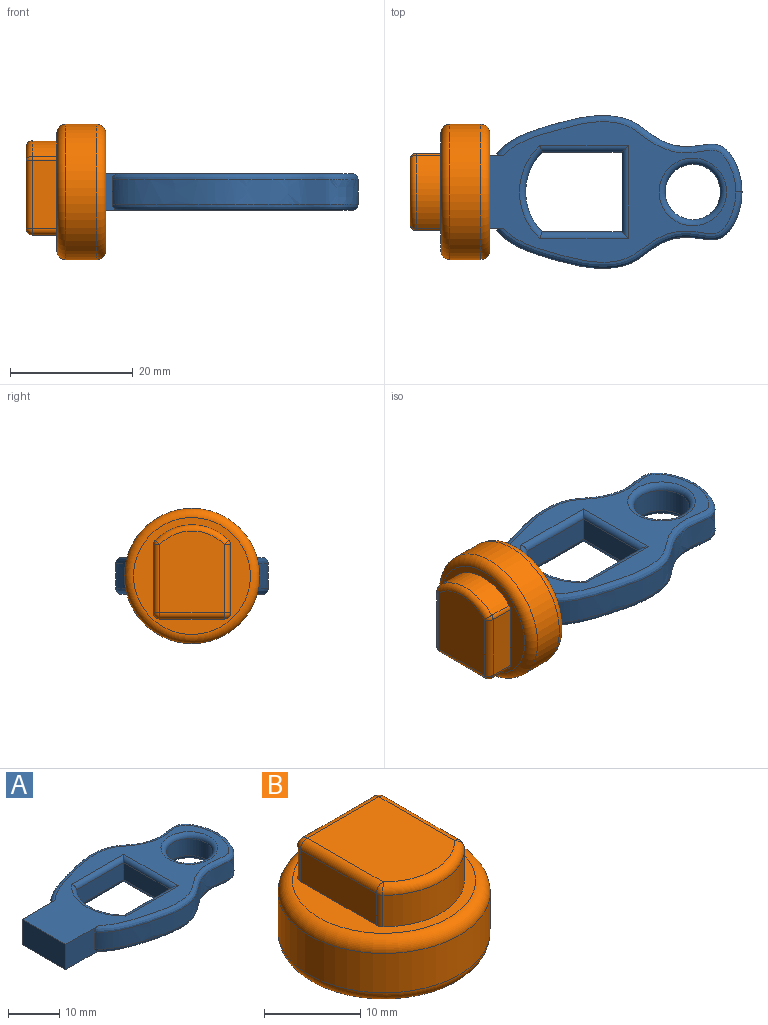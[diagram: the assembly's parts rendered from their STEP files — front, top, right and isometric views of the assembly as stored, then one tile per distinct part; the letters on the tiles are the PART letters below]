
ASSEMBLY  parts=2 mates=1
PART A: 26 faces, bbox 48.4x25.2x6.4 mm
  f0: plane 12x6mm, normal (-1,0,0), area 72mm2, adj f1,f9,f10,f11
  f1: plane 9.62x6.37mm, normal (0,-1,0), area 48.5mm2, adj f0,f2,f10,f11,f12,f19
  f2: extruded ~40x12.43mm, area 192.2mm2, adj f1,f3,f12,f19
  f3: extruded ~40x12.43mm, area 192.2mm2, adj f2,f9,f13,f20
  f4: plane 13x4mm, normal (0,-1,0), area 52mm2, adj f5,f8,f16,f23
  f5: plane 13x4mm, normal (-1,0,0), area 52mm2, adj f4,f6,f15,f22
  f6: plane 13x4mm, normal (0,1,0), area 52mm2, adj f5,f8,f17,f24
  f7: cylinder r=4.5mm len=9mm, axis (0,0,-1), area 113.1mm2, adj f14,f21
  f8: cylinder r=9.19mm len=13mm, axis (0,0,-1), area 57.8mm2, adj f4,f6,f18,f25
  f9: plane 9.62x6.37mm, normal (0,1,0), area 48.5mm2, adj f0,f3,f10,f11,f13,f20
  f10: plane 47x22.86mm, normal (0,0,1), area 414.5mm2, adj f0,f1,f9,f19,f20,f21,f22,f23
  f11: plane 47x22.86mm, normal (0,0,-1), area 414.5mm2, adj f0,f1,f9,f12,f13,f14,f15,f16
  f12: bspline ~40.69x12.66mm, area 73.4mm2, adj f1,f2,f11,f13
  f13: bspline ~40.69x12.66mm, area 73.4mm2, adj f3,f9,f11,f12
  f14: torus R=5.5mm, axis (0,0,1), area 48mm2, adj f7,f11
  f15: cylinder r=1mm len=15mm, axis (0,-1,0), area 22mm2, adj f5,f11,f16,f17
  f16: cylinder r=1mm len=14.4mm, axis (1,0,0), area 21.5mm2, adj f4,f11,f15,f18
  f17: cylinder r=1mm len=14.4mm, axis (-1,0,0), area 21.5mm2, adj f6,f11,f15,f18
  f18: torus R=10.19mm, axis (0,0,1), area 24.2mm2, adj f8,f11,f16,f17
  f19: bspline ~40.69x12.66mm, area 73.4mm2, adj f1,f2,f10,f20
  f20: bspline ~40.69x12.66mm, area 73.4mm2, adj f3,f9,f10,f19
  f21: torus R=5.5mm, axis (0,0,1), area 48mm2, adj f7,f10
  f22: cylinder r=1mm len=15mm, axis (0,1,0), area 22mm2, adj f5,f10,f23,f24
  f23: cylinder r=1mm len=14.4mm, axis (-1,0,0), area 21.5mm2, adj f4,f10,f22,f25
  f24: cylinder r=1mm len=14.4mm, axis (1,0,0), area 21.5mm2, adj f6,f10,f22,f25
  f25: torus R=10.19mm, axis (0,0,1), area 24.2mm2, adj f8,f10,f23,f24
PART B: 27 faces, bbox 23.8x23.8x13 mm
  f0: plane 11.11x4mm, normal (-1,0,0), area 44.4mm2, adj f5,f15,f17,f18
  f1: cylinder r=8.33mm len=11.93mm, axis (0,0,-1), area 53.2mm2, adj f5,f17,f23,f26
  f2: plane 11.11x4mm, normal (1,0,0), area 44.4mm2, adj f5,f20,f24,f26
  f3: plane 10.5x4mm, normal (0,1,0), area 42mm2, adj f5,f15,f19,f20
  f4: plane 13.33x10.5mm, normal (0,0,1), area 132.7mm2, adj f18,f19,f23,f24
  f5: plane 19x19mm, normal (0,0,1), area 103.3mm2, adj f0,f1,f2,f3,f13,f15,f17,f20
  f6: plane 19x19mm, normal (0,0,-1), area 202.3mm2, adj f8,f9,f10,f11,f14
  f7: cylinder r=11mm len=22mm, axis (0,0,1), area 345.6mm2, adj f13,f14
  f8: plane 7x6.5mm, normal (-1,0,0), area 45.5mm2, adj f6,f9,f11,f12
  f9: plane 12.5x7mm, normal (0,1,0), area 87.5mm2, adj f6,f8,f10,f12
  f10: plane 7x6.5mm, normal (1,0,0), area 45.5mm2, adj f6,f9,f11,f12
  f11: plane 12.5x7mm, normal (0,-1,0), area 87.5mm2, adj f6,f8,f10,f12
  f12: plane 12.5x6.5mm, normal (0,0,-1), area 81.2mm2, adj f8,f9,f10,f11
  f13: torus R=9.5mm, axis (0,0,1), area 154.8mm2, adj f5,f7
  f14: torus R=9.5mm, axis (0,0,1), area 154.8mm2, adj f6,f7
  f15: cylinder r=1mm len=4mm, axis (0,0,-1), area 6.3mm2, adj f0,f3,f5,f16
  f16: sphere r=1mm, area 1.6mm2, adj f15,f18,f19
  f17: cylinder r=1mm len=4mm, axis (0,0,-1), area 3.1mm2, adj f0,f1,f5,f21
  f18: cylinder r=1mm len=11.11mm, axis (0,1,0), area 17.4mm2, adj f0,f4,f16,f21
  f19: cylinder r=1mm len=10.5mm, axis (1,0,0), area 16.5mm2, adj f3,f4,f16,f22
  f20: cylinder r=1mm len=4mm, axis (0,0,1), area 6.3mm2, adj f2,f3,f5,f22
  f21: sphere r=1mm, area 0.8mm2, adj f17,f18,f23
  f22: sphere r=1mm, area 1.6mm2, adj f19,f20,f24
  f23: torus R=7.33mm, axis (0,0,1), area 20mm2, adj f1,f4,f21,f25
  f24: cylinder r=1mm len=11.11mm, axis (0,-1,0), area 17.4mm2, adj f2,f4,f22,f25
  f25: sphere r=1mm, area 0.8mm2, adj f23,f24,f26
  f26: cylinder r=1mm len=4mm, axis (0,0,-1), area 3.1mm2, adj f1,f2,f5,f25
PLACE A t=(-19.67,-1.01,-9.27)mm fixed
PLACE B rot(axis=(-0.58,-0.58,0.58),120deg) t=(-20.67,-1.01,-6.27)mm
MATE fastened A.f0 <-> B.f7  axis (-1,0,0) through (-19.67,-1.01,-6.27)mm
